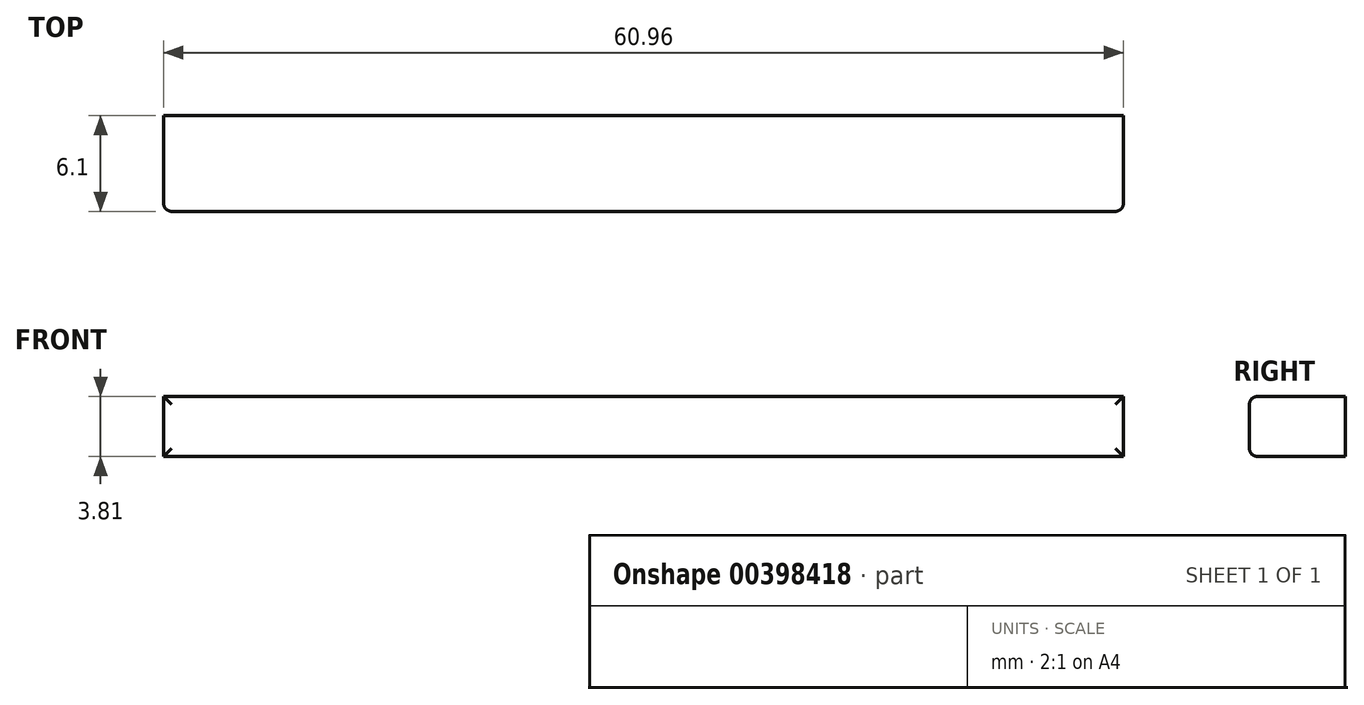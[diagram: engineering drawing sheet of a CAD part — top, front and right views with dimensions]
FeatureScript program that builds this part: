
annotation { "Feature Type Name" : "Feature", "Feature Type Description" : "" }
export const myFeature = defineFeature(function(context is Context, id is Id, definition is map)
    precondition{}
    {
        {
            var Q0;
            Q0=qCreatedBy(makeId("Top.planeOp"),FACE);
            var sketch = newSketch(context, id + "F0", { "sketchPlane" : qUnion([Q0])});
            skLineSegment(sketch, "E0.bottom", {"start": v(0, 0) * mm, "end": v(60.96, 0) * mm});
            skLineSegment(sketch, "E0.top", {"start": v(0, -6.1) * mm, "end": v(60.96, -6.1) * mm});
            skLineSegment(sketch, "E0.left", {"start": v(0, 0) * mm, "end": v(0, -6.1) * mm});
            skLineSegment(sketch, "E0.right", {"start": v(60.96, 0) * mm, "end": v(60.96, -6.1) * mm});
            skSolve(sketch);
        }
        {
            var Q0;
            Q0=makeQuery(id+"F0.imprint","IMPRINT",FACE,{"disambiguationData":[TD([[makeQuery(id+"F0.imprint","IMPRINT",EDGE,{"derivedFrom":sQuery(id+"F0.wireOp",EDGE,"E0.bottom")}),-1.0]])]});
            extrude(context, id + "F1", {"entities" : qUnion([Q0]), "depth" : 3.8 * mm});
        }
        {
            var Q0;
            Q0=makeQuery(id+"F1.opExtrude","CAP_EDGE",EDGE,{"disambiguationData":[OSD([sQuery(id+"F0.wireOp",EDGE,"E0.top")])],"isStart":false});
            var Q1;
            Q1=makeQuery(id+"F1.opExtrude","CAP_EDGE",EDGE,{"disambiguationData":[OSD([sQuery(id+"F0.wireOp",EDGE,"E0.top")])],"isStart":true});
            var Q2;
            Q2=makeQuery(id+"F1.opExtrude","SWEPT_EDGE",EDGE,{"disambiguationData":[OSD([sQuery(id+"F0.wireOp",EDGE,"E0.top"),sQuery(id+"F0.wireOp",EDGE,"E0.right")])]});
            var Q3;
            Q3=makeQuery(id+"F1.opExtrude","SWEPT_EDGE",EDGE,{"disambiguationData":[OSD([sQuery(id+"F0.wireOp",EDGE,"E0.top"),sQuery(id+"F0.wireOp",EDGE,"E0.left")])]});
            fillet(context, id + "F2", {"entities" : qUnion([Q0, Q1, Q2, Q3]), "radius" : 0.5 * mm, "tangentPropagation" : true, "allowEdgeOverflow" : false});
        }
    });
